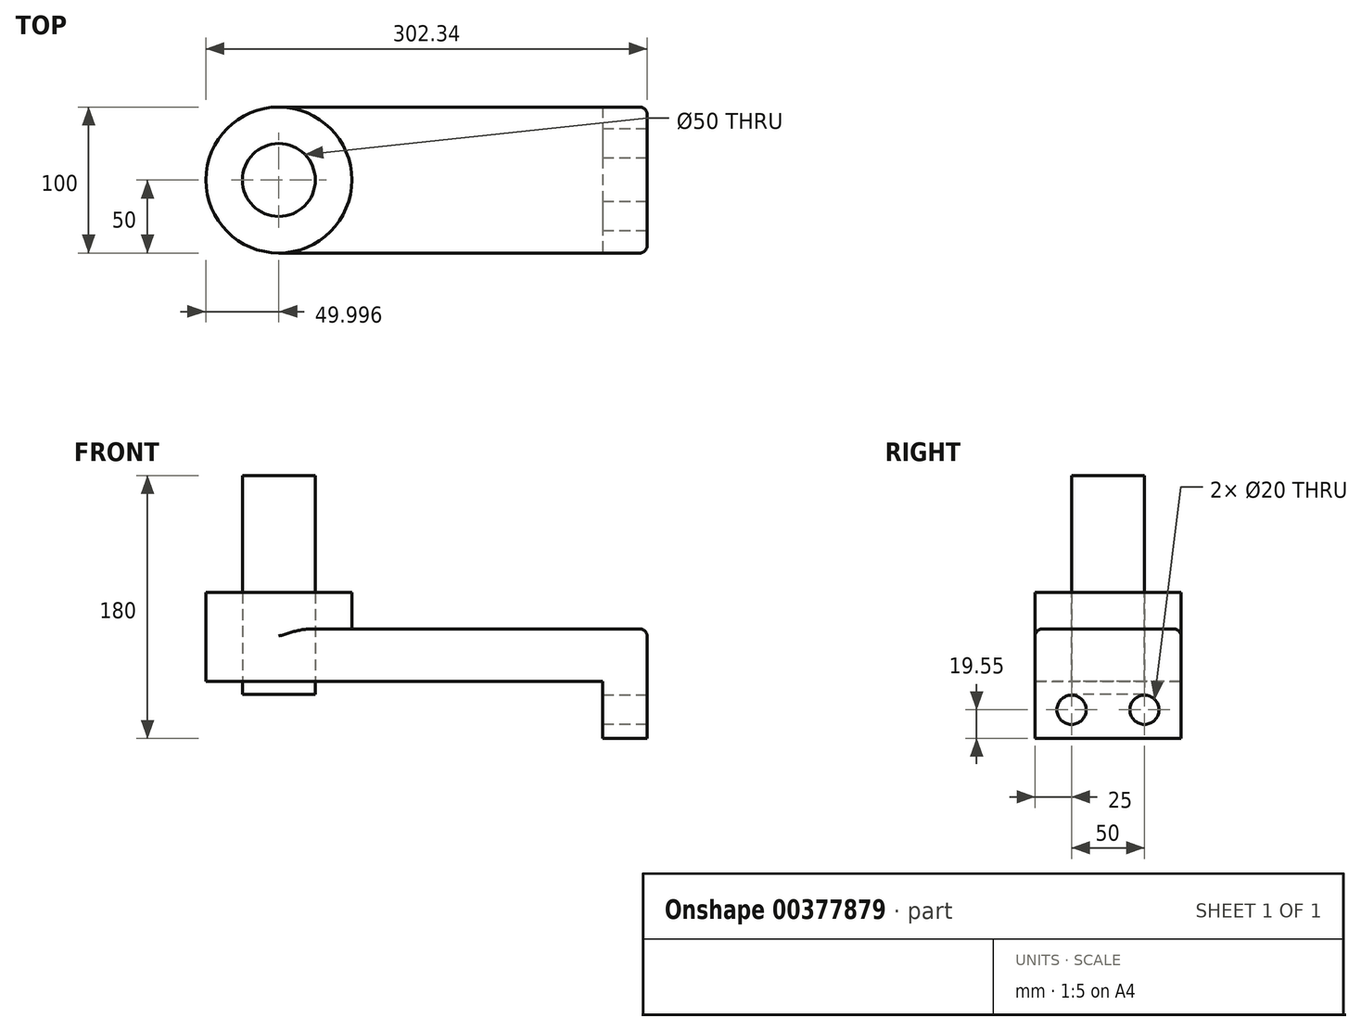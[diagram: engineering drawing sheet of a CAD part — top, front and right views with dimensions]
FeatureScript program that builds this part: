
annotation { "Feature Type Name" : "Feature", "Feature Type Description" : "" }
export const myFeature = defineFeature(function(context is Context, id is Id, definition is map)
    precondition{}
    {
        {
            var Q0;
            Q0=qCreatedBy(makeId("Front.planeOp"),FACE);
            var sketch = newSketch(context, id + "F0", { "sketchPlane" : qUnion([Q0])});
            skLineSegment(sketch, "E0.bottom", {"start": v(110.92, -50) * mm, "end": v(-110.92, -50) * mm});
            skLineSegment(sketch, "E0.top", {"start": v(110.92, 50) * mm, "end": v(-110.92, 50) * mm});
            skLineSegment(sketch, "E0.left", {"start": v(110.92, -50) * mm, "end": v(110.92, 50) * mm});
            skLineSegment(sketch, "E0.right", {"start": v(-110.92, -50) * mm, "end": v(-110.92, 50) * mm});
            skPoint(sketch, "E0.middle", {"position": v(0, 0) * mm});
            skCircle(sketch, "E1", {"center": v(-110.92, 0) * mm, "radius": 50 * mm});
            skCircle(sketch, "E2", {"center": v(-110.92, 0) * mm, "radius": 25 * mm});
            skSolve(sketch);
        }
        {
            var Q0;
            Q0 = qSketchRegion(id + "F0", true);
            extrude(context, id + "F1", {"entities" : qUnion([Q0]), "depth" : 35.9 * mm});
        }
        {
            var Q0;
            {var subQ1=sQuery(id+"F0.wireOp",EDGE,"E0.right");var subQ3=sQuery(id+"F0.wireOp",EDGE,"E2");var subQ4=makeQuery(id+"F0.imprint","INTERSECT",VERTEX,{"disambiguationData":[OD(0.0)],"derivedFrom":[subQ1,subQ3]});Q0=makeQuery(id+"F0.imprint","IMPRINT",FACE,{"disambiguationData":[TD([[makeQuery(id+"F0.imprint","IMPRINT",EDGE,{"disambiguationData":[TD([[subQ4,-1.0]])],"derivedFrom":subQ3}),-1.0]])]});}
            var Q1;
            {var subQ1=sQuery(id+"F0.wireOp",EDGE,"E0.right");var subQ3=sQuery(id+"F0.wireOp",EDGE,"E2");var subQ4=makeQuery(id+"F0.imprint","INTERSECT",VERTEX,{"disambiguationData":[OD(0.0)],"derivedFrom":[subQ1,subQ3]});Q1=makeQuery(id+"F0.imprint","IMPRINT",FACE,{"disambiguationData":[TD([[makeQuery(id+"F0.imprint","IMPRINT",EDGE,{"disambiguationData":[TD([[subQ4,1.0]])],"derivedFrom":subQ3}),-1.0]])]});}
            extrude(context, id + "F2", {"entities" : qUnion([Q0, Q1]), "operationType" : NewBodyOperationType.ADD, "oppositeDirection" : true, "depth" : 25 * mm});
        }
        {
            var Q0;
            Q0=makeQuery(id+"F1.opExtrude","SWEPT_FACE",FACE,{"disambiguationData":[OSD([sQuery(id+"F0.wireOp",EDGE,"E0.left")])]});
            var sketch = newSketch(context, id + "F3", { "sketchPlane" : qUnion([Q0])});
            skLineSegment(sketch, "E3.bottom", {"start": v(0, 50) * mm, "end": v(-75, 50) * mm});
            skLineSegment(sketch, "E3.top", {"start": v(0, -50) * mm, "end": v(-75, -50) * mm});
            skLineSegment(sketch, "E3.left", {"start": v(0, 50) * mm, "end": v(0, -50) * mm});
            skLineSegment(sketch, "E3.right", {"start": v(-75, 50) * mm, "end": v(-75, -50) * mm});
            skCircle(sketch, "E4", {"center": v(-55.45, 25) * mm, "radius": 10 * mm});
            skLineSegment(sketch, "E5", {"start": v(-35.9, 0) * mm, "end": v(-75, 0) * mm});
            skCircle(sketch, "E6.MirrorC", {"center": v(-55.45, -25) * mm, "radius": 10 * mm});
            skSolve(sketch);
        }
        {
            var Q0;
            Q0 = qSketchRegion(id + "F3", true);
            extrude(context, id + "F4", {"entities" : qUnion([Q0]), "operationType" : NewBodyOperationType.ADD, "depth" : 30.5 * mm});
        }
        {
            var Q0;
            Q0=makeQuery(id+"F2.opExtrude","CAP_EDGE",EDGE,{"disambiguationData":[OSD([sQuery(id+"F0.wireOp",EDGE,"E1")])],"isStart":true});
            var Q1;
            Q1=makeQuery(id+"F4.opExtrude","CAP_EDGE",EDGE,{"disambiguationData":[OSD([sQuery(id+"F3.wireOp",EDGE,"E3.left")])],"isStart":false});
            var Q2;
            Q2=makeQuery(id+"F4.boolean.opBoolean","MERGE",EDGE,{"derivedFrom":[makeQuery(id+"F1.opExtrude","CAP_EDGE",EDGE,{"disambiguationData":[OSD([sQuery(id+"F0.wireOp",EDGE,"E0.top")])],"isStart":true}),makeQuery(id+"F4.opExtrude","SWEPT_EDGE",EDGE,{"disambiguationData":[OSD([sQuery(id+"F3.wireOp",EDGE,"E3.bottom"),sQuery(id+"F3.wireOp",EDGE,"E3.left")])]})]});
            var Q3;
            Q3=makeQuery(id+"F4.opExtrude","CAP_EDGE",EDGE,{"disambiguationData":[OSD([sQuery(id+"F3.wireOp",EDGE,"E3.bottom")])],"isStart":false});
            var Q4;
            Q4=makeQuery(id+"F4.opExtrude","CAP_EDGE",EDGE,{"disambiguationData":[OSD([sQuery(id+"F3.wireOp",EDGE,"E3.top")])],"isStart":false});
            var Q5;
            Q5=makeQuery(id+"F4.boolean.opBoolean","MERGE",EDGE,{"derivedFrom":[makeQuery(id+"F1.opExtrude","CAP_EDGE",EDGE,{"disambiguationData":[OSD([sQuery(id+"F0.wireOp",EDGE,"E0.bottom")])],"isStart":true}),makeQuery(id+"F4.opExtrude","SWEPT_EDGE",EDGE,{"disambiguationData":[OSD([sQuery(id+"F3.wireOp",EDGE,"E3.top"),sQuery(id+"F3.wireOp",EDGE,"E3.left")])]})]});
            fillet(context, id + "F5", {"entities" : qUnion([Q0, Q1, Q2, Q3, Q4, Q5]), "radius" : 5 * mm, "tangentPropagation" : true, "allowEdgeOverflow" : false});
        }
        {
            var Q0;
            Q0=makeQuery(id+"F1.opExtrude","SWEPT_BODY",BODY,{"disambiguationData":[OSD([sQuery(id+"F0.wireOp",EDGE,"E0.bottom"),sQuery(id+"F0.wireOp",EDGE,"E0.top"),sQuery(id+"F0.wireOp",EDGE,"E0.left"),sQuery(id+"F0.wireOp",EDGE,"E1"),sQuery(id+"F0.wireOp",EDGE,"E2")])]});
            var Q1;
            {var subQ0=sQuery(id+"F3.wireOp",EDGE,"E3.bottom");var subQ1=sQuery(id+"F0.wireOp",EDGE,"E0.top");Q1=makeQuery(id+"F5.opFillet","BLEND_EDGE",EDGE,{"blendedFrom":[makeQuery(id+"F4.boolean.opBoolean","MERGE",EDGE,{"derivedFrom":[makeQuery(id+"F1.opExtrude","CAP_EDGE",EDGE,{"disambiguationData":[OSD([subQ1])],"isStart":true}),makeQuery(id+"F4.opExtrude","SWEPT_EDGE",EDGE,{"disambiguationData":[OSD([subQ0,sQuery(id+"F3.wireOp",EDGE,"E3.left")])]})]}),makeQuery(id+"F4.boolean.opBoolean","MERGE",FACE,{"derivedFrom":[makeQuery(id+"F1.opExtrude","SWEPT_FACE",FACE,{"disambiguationData":[OSD([subQ1])]}),makeQuery(id+"F4.opExtrude","SWEPT_FACE",FACE,{"disambiguationData":[OSD([subQ0])]})]})],"blendedInto":[makeQuery(id+"F4.boolean.opBoolean","MERGE",FACE,{"derivedFrom":[makeQuery(id+"F1.opExtrude","SWEPT_FACE",FACE,{"disambiguationData":[OSD([subQ1])]}),makeQuery(id+"F4.opExtrude","SWEPT_FACE",FACE,{"disambiguationData":[OSD([subQ0])]})]})]});}
            transform(context, id + "F6", {"entities" : qUnion([Q0]), "transformType" : TransformType.ROTATION, "transformAxis" : qUnion([Q1]), "angle" : 270 * degree, "makeCopy" : false});
        }
        {
            var Q0;
            Q0=makeQuery(id+"F2.opExtrude","CAP_FACE",FACE,{"disambiguationData":[OSD([sQuery(id+"F0.wireOp",EDGE,"E1"),sQuery(id+"F0.wireOp",EDGE,"E2")])],"isStart":false});
            var sketch = newSketch(context, id + "F7", { "sketchPlane" : qUnion([Q0])});
            skCircle(sketch, "E7", {"center": v(-110.92, 45) * mm, "radius": 25 * mm});
            skPoint(sketch, "E7.first.point", {"position": v(-90, 31.33) * mm});
            skPoint(sketch, "E7.second.point", {"position": v(-135.22, 39.09) * mm});
            skPoint(sketch, "E7.third.point", {"position": v(-135.22, 39.09) * mm});
            skSolve(sketch);
        }
        {
            var Q0;
            Q0 = qSketchRegion(id + "F7", true);
            extrude(context, id + "F8", {"entities" : qUnion([Q0]), "depth" : 150 * mm});
        }
        {
            var Q0;
            Q0=makeQuery(id+"F8.opExtrude","SWEPT_BODY",BODY,{"disambiguationData":[OSD([sQuery(id+"F7.wireOp",EDGE,"E7")])]});
            var Q1;
            Q1=makeQuery(id+"F8.opExtrude","CAP_EDGE",EDGE,{"disambiguationData":[OSD([sQuery(id+"F7.wireOp",EDGE,"E7")])],"isStart":false});
            transform(context, id + "F9", {"entities" : qUnion([Q0]), "transformType" : TransformType.TRANSLATION_3D, "dx" : 0 * mm, "dy" : 0 * mm, "dz" : -70 * mm, "makeCopy" : false});
        }
    });
